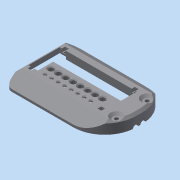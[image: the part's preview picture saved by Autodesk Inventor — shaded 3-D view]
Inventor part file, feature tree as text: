
AUTODESK INVENTOR PART (.ipt)
format: ipt  version: 2014 SP1 (Build 180222100, 222)  size: 738,304 bytes
history: native  units: in
note: dims shown in document units (in); Inventor stores cm internally (conversion verified against a paired STEP export)
features: extrude x14, sketch x14, projected_geometry x14, chamfer x8, other x4, fillet x3, move_body x1, plane x1
ambient origin geometry x8: Origin, YZ Plane, XZ Plane, XY Plane, X Axis, Y Axis, Z Axis, Center Point
bodies: Solid1 (feature_tree)
feature tree (59):
  other  "electronicsbox_top.ipt"
  other  "tm1638module.ipt"
  move_body  "Move Body1"
  plane  "Work Plane1"
  extrude  "Extrusion1"  Depth=0.3937in
  extrude  "Extrusion2"  Depth=0.1875in
  extrude  "sketch"  Depth=0.1875in
  extrude  "Extrusion4"  Depth=0.25in TaperAngle=0.0deg
  chamfer  "Chamfer2"  Distance=0.1in
  sketch  "Sketch7"  dims[d12=0.2756in]
  extrude  "Extrusion8"  Depth=0.1969in
  extrude  "Extrusion9"  Depth=0.1969in TaperAngle=0.0deg
  chamfer  "Chamfer4"  Distance=0.5in
  chamfer  "Chamfer5"  Distance=0.05in
  extrude  "Extrusion10"  Depth=0.1969in
  extrude  "Extrusion11"  Depth=0.1969in
  extrude  "Extrusion12"  Depth=0.1969in
  chamfer  "Chamfer6"  Distance=0.025in
  chamfer  "Chamfer7"  Distance=0.0625in
  fillet  "Fillet2"  Radius=0.05in
  extrude  "Extrusion18"  Depth=0.1969in TaperAngle=45.0deg
  chamfer  "Chamfer9"  Distance=0.125in
  fillet  "Fillet5"  Radius=0.385in
  extrude  "Extrusion19"  Depth=0.1969in
  extrude  "Extrusion20"  Depth=0.1969in TaperAngle=0.0deg
  fillet  "Fillet6"  Radius=0.125in
  extrude  "Extrusion21"  Depth=0.1969in
  extrude  "Extrusion22"  Depth=0.1969in
  chamfer  "Chamfer10"  Distance=0.125in
  chamfer  "Chamfer12"  Distance=0.375in
  sketch  "Sketch6"  dims[d11=0.2756in]
  other  "Solid1::tm1638module.ipt"
  other  "TaggingFeature1"
  sketch  "Sketch2"  dims[d0=0.3937in d1=0.3937in]
  sketch  "Sketch3"  dims[d2=2.0in d3=0.0in d4=1.0in d5=0.1875in]
  projected_geometry  "Projected Loop1"
  projected_geometry  "Projected Loop2"
  projected_geometry  "Projected Loop3"
  projected_geometry  "Projected Loop4"
  projected_geometry  "Projected Loop5"
  projected_geometry  "Projected Loop6"
  projected_geometry  "Projected Loop7"
  projected_geometry  "Projected Loop8"
  projected_geometry  "Projected Loop9"
  projected_geometry  "Projected Loop10"
  projected_geometry  "Projected Loop11"
  sketch  "Sketch4"  dims[d6=0.1875in d7=0.1875in]
  sketch  "Sketch5"  dims[d8=0.1875in d9=0.25in d10=0.0in]
  sketch  "Sketch9"  dims[d13=0.2756in]
  sketch  "Sketch10"  dims[d14=0.2756in]
  projected_geometry  "Projected Loop12"
  projected_geometry  "Projected Loop13"
  sketch  "Sketch11"  dims[d15=0.2756in]
  sketch  "Sketch12"  dims[d16=0.2756in]
  sketch  "Sketch18"  dims[d17=0.2756in]
  projected_geometry  "Projected Loop14"
  sketch  "Sketch20"  dims[d18=0.2756in]
  sketch  "Sketch21"  dims[d19=0.05in]
  sketch  "Sketch22"  dims[d20=0.05in d21=0.1in d22=0.05in d23=0.4in d24=0.0in d25=0.5in d26=0.0in d27=0.05in d28=0.025in d29=0.025in d30=0.025in d31=0.025in d35=0.0625in d36=0.0in d37=0.05in d38=0.125in d39=45.0deg d50=0.125in d51=0.125in d52=45.0deg d53=0.125in d54=0.0in d55=0.385in d56=0.385in d57=0.125in d58=0.0in d59=0.125in d60=0.125in d61=45.0deg d62=0.375in d63=0.125in d64=0.125in d65=0.375in d66=0.125in d67=0.0in d68=0.2756in d69=0.2756in d70=0.1969in d71=0.1969in d72=1.0in d73=0.0in d74=0.075in d75=0.075in d76=0.1in d77=0.1in d78=0.222in d79=0.0in d93=0.1in d94=0.125in d95=45.0deg d96=0.05in d97=0.125in d98=45.0deg d99=0.075in d111=0.75in d112=0.5in d113=0.0in d114=0.25in d115=0.125in d116=45.0deg d117=0.125in d119=0.25in d120=0.25in d121=0.25in d122=0.1625in d123=0.0in d124=0.75in d125=0.2in d126=0.0in d127=0.25in d128=0.0312in d129=0.2362in d130=0.0in d131=0.1969in d132=0.1969in d133=0.1969in d134=0.1969in d135=0.1969in d136=0.1969in d137=0.1969in d138=0.1969in d139=0.1772in d140=0.0in d141=0.15in d142=0.125in d143=45.0deg d147=0.0394in d148=0.125in d149=45.0deg]
